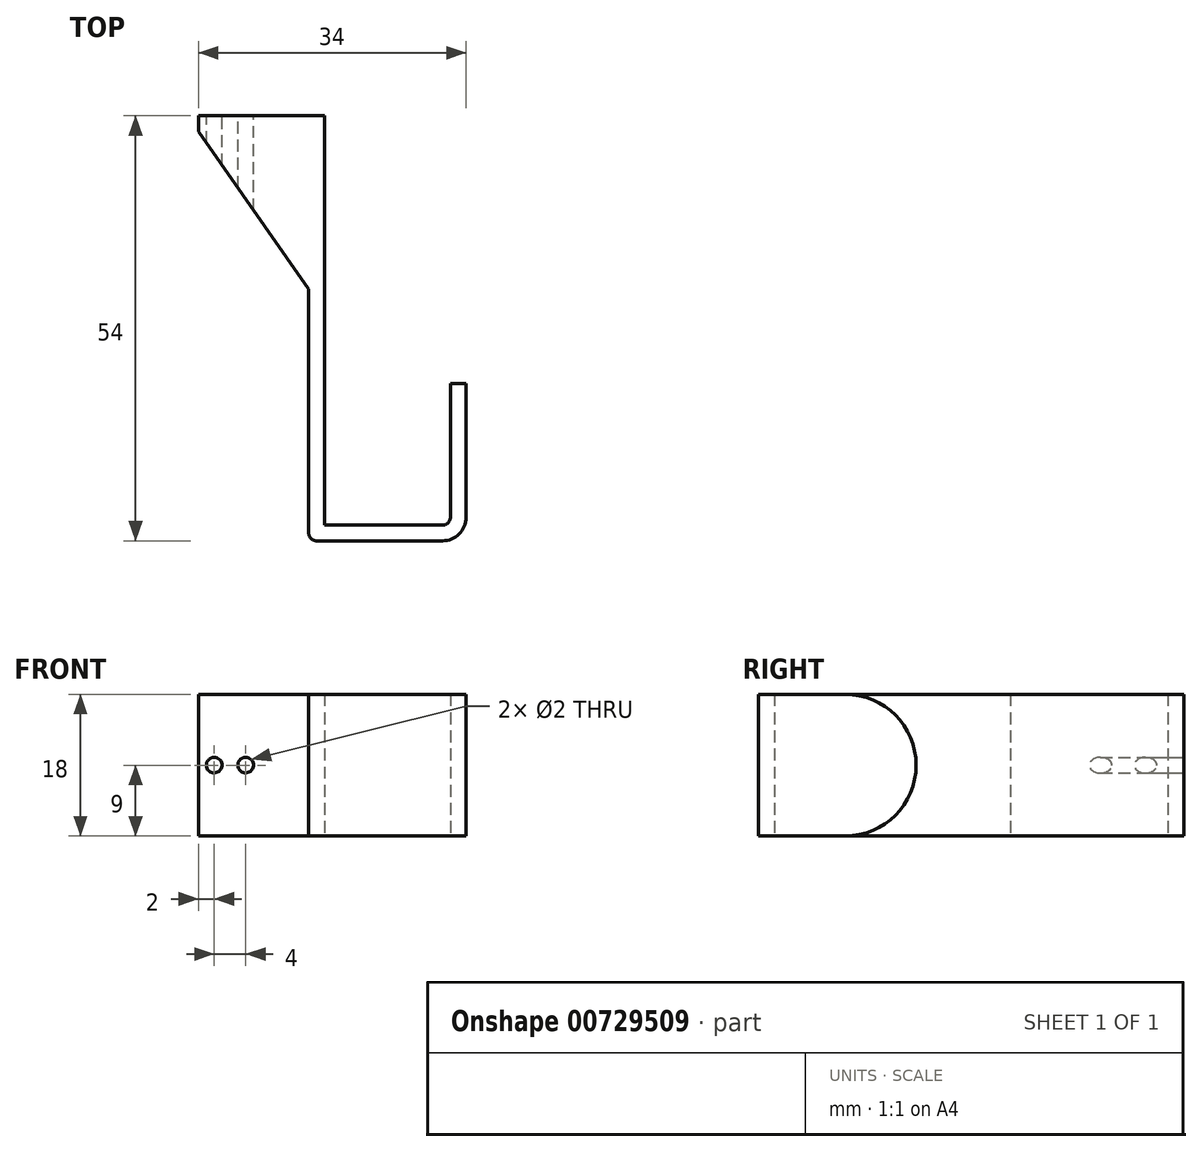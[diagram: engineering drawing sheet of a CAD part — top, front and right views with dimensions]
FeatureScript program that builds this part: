
annotation { "Feature Type Name" : "Feature", "Feature Type Description" : "" }
export const myFeature = defineFeature(function(context is Context, id is Id, definition is map)
    precondition{}
    {
        {
            var Q0;
            Q0=qCreatedBy(makeId("Top.planeOp"),FACE);
            var sketch = newSketch(context, id + "F0", { "sketchPlane" : qUnion([Q0])});
            skLineSegment(sketch, "E0.bottom", {"start": v(-1, -25) * mm, "end": v(1, -25) * mm});
            skLineSegment(sketch, "E0.top", {"start": v(-1, 25) * mm, "end": v(1, 25) * mm});
            skLineSegment(sketch, "E0.left", {"start": v(-1, -25) * mm, "end": v(-1, 25) * mm});
            skLineSegment(sketch, "E0.right", {"start": v(1, -25) * mm, "end": v(1, 25) * mm});
            skPoint(sketch, "E1", {"position": v(0, 25) * mm});
            skPoint(sketch, "E2", {"position": v(1, 0) * mm});
            skLineSegment(sketch, "E3.bottom", {"start": v(-1, -25) * mm, "end": v(19, -25) * mm});
            skLineSegment(sketch, "E3.top", {"start": v(-1, -27) * mm, "end": v(19, -27) * mm});
            skLineSegment(sketch, "E3.left", {"start": v(-1, -25) * mm, "end": v(-1, -27) * mm});
            skLineSegment(sketch, "E3.right", {"start": v(19, -25) * mm, "end": v(19, -27) * mm});
            skLineSegment(sketch, "E4.bottom", {"start": v(19, -25) * mm, "end": v(17, -25) * mm});
            skLineSegment(sketch, "E4.top", {"start": v(19, -7) * mm, "end": v(17, -7) * mm});
            skLineSegment(sketch, "E4.left", {"start": v(19, -25) * mm, "end": v(19, -7) * mm});
            skLineSegment(sketch, "E4.right", {"start": v(17, -25) * mm, "end": v(17, -7) * mm});
            skLineSegment(sketch, "E5.bottom", {"start": v(1, 25) * mm, "end": v(-15, 25) * mm});
            skLineSegment(sketch, "E5.top", {"start": v(1, 27) * mm, "end": v(-15, 27) * mm});
            skLineSegment(sketch, "E5.left", {"start": v(1, 25) * mm, "end": v(1, 27) * mm});
            skLineSegment(sketch, "E5.right", {"start": v(-15, 25) * mm, "end": v(-15, 27) * mm});
            skLineSegment(sketch, "E6", {"start": v(-15, 25) * mm, "end": v(-1, 5) * mm});
            skSolve(sketch);
        }
        {
            var Q0;
            Q0 = qSketchRegion(id + "F0", true);
            extrude(context, id + "F1", {"entities" : qUnion([Q0]), "depth" : 18 * mm, "offsetDistance" : 25 * mm});
        }
        {
            var Q0;
            Q0=makeQuery(id+"F1.opExtrude","SWEPT_FACE",FACE,{"disambiguationData":[OSD([sQuery(id+"F0.wireOp",EDGE,"E5.top")])]});
            var sketch = newSketch(context, id + "F2", { "sketchPlane" : qUnion([Q0])});
            skLineSegment(sketch, "E7", {"start": v(-1, 9) * mm, "end": v(15, 9) * mm, "construction": true});
            skPoint(sketch, "E8", {"position": v(9, 9) * mm});
            skPoint(sketch, "E9", {"position": v(13, 9) * mm});
            skCircle(sketch, "E10", {"center": v(9, 9) * mm, "radius": 1 * mm});
            skCircle(sketch, "E11", {"center": v(13, 9) * mm, "radius": 1 * mm});
            skSolve(sketch);
        }
        {
            var Q0;
            Q0 = qSketchRegion(id + "F2", true);
            extrude(context, id + "F3", {"entities" : qUnion([Q0]), "operationType" : NewBodyOperationType.REMOVE, "oppositeDirection" : true, "depth" : 25 * mm, "offsetDistance" : 25 * mm});
        }
        {
            var Q0;
            Q0=makeQuery(id+"F1.opExtrude","SWEPT_EDGE",EDGE,{"disambiguationData":[OSD([sQuery(id+"F0.wireOp",EDGE,"E3.top"),sQuery(id+"F0.wireOp",EDGE,"E3.right")])]});
            fillet(context, id + "F4", {"entities" : qUnion([Q0]), "radius" : 3 * mm, "tangentPropagation" : true, "allowEdgeOverflow" : false});
        }
        {
            var Q0;
            Q0=makeQuery(id+"F1.opExtrude","SWEPT_EDGE",EDGE,{"disambiguationData":[OSD([sQuery(id+"F0.wireOp",EDGE,"E3.bottom"),sQuery(id+"F0.wireOp",EDGE,"E4.bottom"),sQuery(id+"F0.wireOp",EDGE,"E4.right")])]});
            fillet(context, id + "F5", {"entities" : qUnion([Q0]), "radius" : 1 * mm, "tangentPropagation" : true, "allowEdgeOverflow" : false});
        }
        {
            var Q0;
            Q0=makeQuery(id+"F1.opExtrude","SWEPT_EDGE",EDGE,{"disambiguationData":[OSD([sQuery(id+"F0.wireOp",EDGE,"E3.top"),sQuery(id+"F0.wireOp",EDGE,"E3.left")])]});
            fillet(context, id + "F6", {"entities" : qUnion([Q0]), "radius" : 1 * mm, "tangentPropagation" : true, "allowEdgeOverflow" : false});
        }
        {
            var Q0;
            Q0=makeQuery(id+"F1.opExtrude","CAP_EDGE",EDGE,{"disambiguationData":[OSD([sQuery(id+"F0.wireOp",EDGE,"E4.top")])],"isStart":false});
            var Q1;
            Q1=makeQuery(id+"F1.opExtrude","CAP_EDGE",EDGE,{"disambiguationData":[OSD([sQuery(id+"F0.wireOp",EDGE,"E4.top")])],"isStart":true});
            fillet(context, id + "F7", {"entities" : qUnion([Q0, Q1]), "radius" : 9 * mm, "tangentPropagation" : true, "allowEdgeOverflow" : false});
        }
    });
